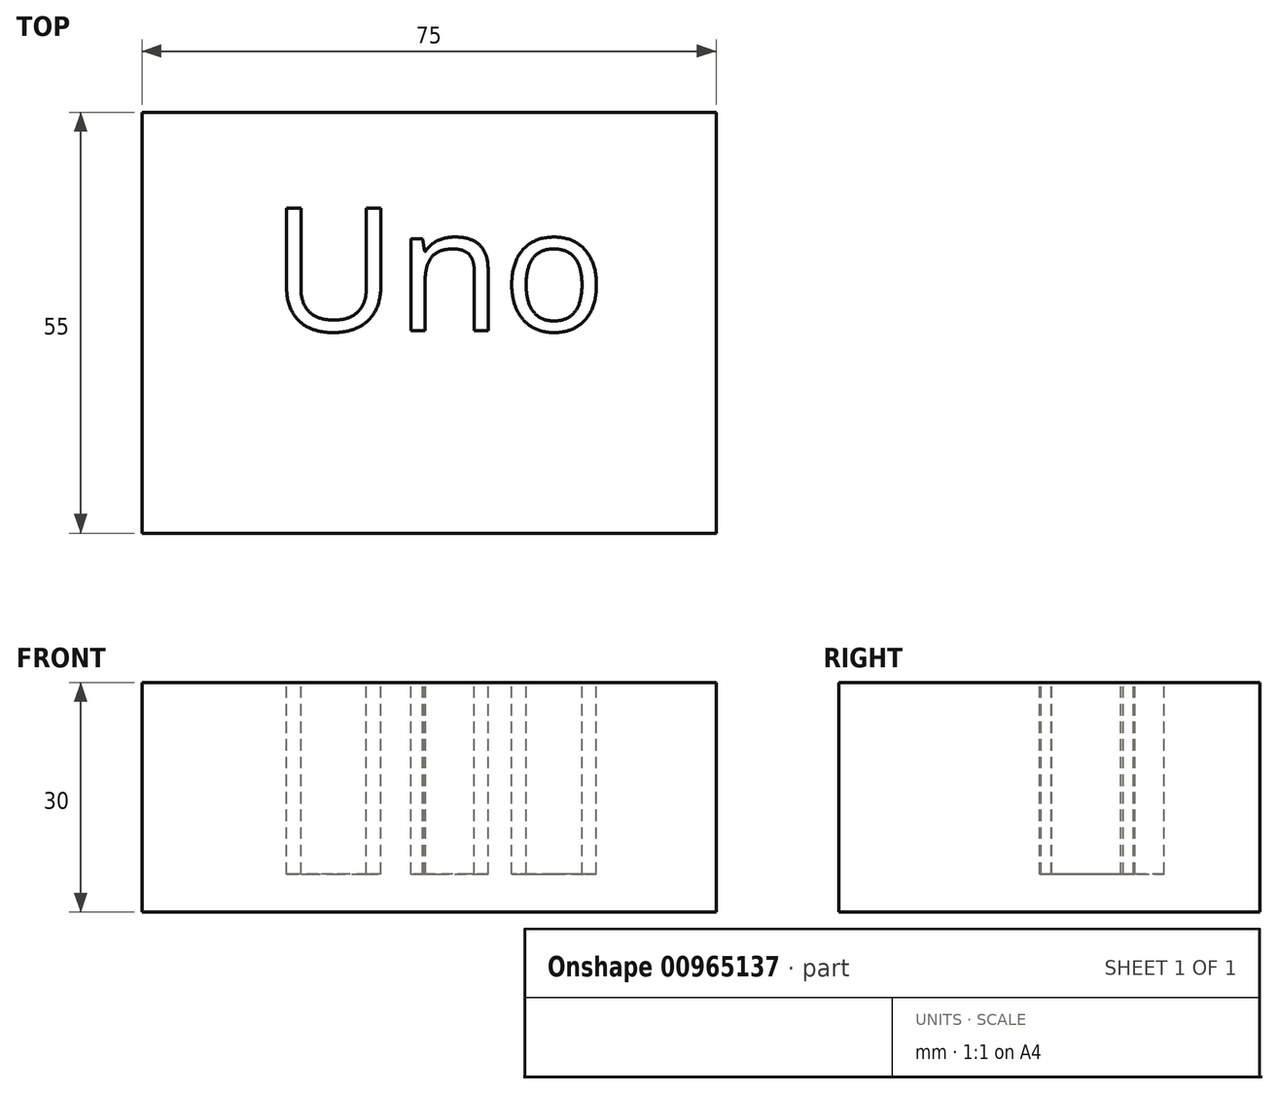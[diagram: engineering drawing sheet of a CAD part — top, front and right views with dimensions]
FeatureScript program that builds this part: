
annotation { "Feature Type Name" : "Feature", "Feature Type Description" : "" }
export const myFeature = defineFeature(function(context is Context, id is Id, definition is map)
    precondition{}
    {
        {
            var Q0;
            Q0=qCreatedBy(makeId("Top.planeOp"),FACE);
            var sketch = newSketch(context, id + "F0", { "sketchPlane" : qUnion([Q0])});
            skLineSegment(sketch, "E0.bottom", {"start": v(-39.25, 33.33) * mm, "end": v(35.75, 33.33) * mm});
            skLineSegment(sketch, "E0.top", {"start": v(-39.25, -21.67) * mm, "end": v(35.75, -21.67) * mm});
            skLineSegment(sketch, "E0.left", {"start": v(-39.25, 33.33) * mm, "end": v(-39.25, -21.67) * mm});
            skLineSegment(sketch, "E0.right", {"start": v(35.75, 33.33) * mm, "end": v(35.75, -21.67) * mm});
            skSolve(sketch);
        }
        {
            var Q0;
            Q0 = qSketchRegion(id + "F0", true);
            extrude(context, id + "F1", {"entities" : qUnion([Q0]), "depth" : 30 * mm, "offsetDistance" : 25 * mm});
        }
        {
            var Q0;
            Q0=makeQuery(id+"F1.opExtrude","CAP_FACE",FACE,{"disambiguationData":[OSD([sQuery(id+"F0.wireOp",EDGE,"E0.bottom"),sQuery(id+"F0.wireOp",EDGE,"E0.top"),sQuery(id+"F0.wireOp",EDGE,"E0.left"),sQuery(id+"F0.wireOp",EDGE,"E0.right")])],"isStart":false});
            var sketch = newSketch(context, id + "F2", { "sketchPlane" : qUnion([Q0])});
            skText(sketch, "E1", { "text": "Uno", "fontName": "OpenSans-Regular.ttf"});
            skLineSegment(sketch, "E2", {"start": v(-39.25, 4.77) * mm, "end": v(35.75, 4.77) * mm});
            const initialGuessF2  = {"E1": [-0.0224, 0.00477, 1, 0, 0.0162]};
            skSetInitialGuess(sketch, initialGuessF2);
            skSolve(sketch);
        }
        {
            var Q0;
            Q0 = qSketchRegion(id + "F2", true);
            extrude(context, id + "F3", {"entities" : qUnion([Q0]), "operationType" : NewBodyOperationType.REMOVE, "oppositeDirection" : true, "depth" : 25 * mm, "offsetDistance" : 25 * mm});
        }
    });
